# Revit family: Lockin Lockers AU_Hybrid Locker_R22
name_source: partatom
category: Furniture
units: mm (PartAtom-declared; Revit-internal decimal feet)

## family parameters
Always vertical = Yes
Cut with Voids When Loaded = No
OmniClass Number = 23.40.20.27
OmniClass Title = Storage Shelving
Render Appearance Source = Family Geometry
Room Calculation Point = No
Shared = Yes
Work Plane-Based = Yes

## types (7) — shared parameters
Base Height Control = 100 mm  [stored 0.328084 ft]
Body/Frame Material = Material - Welded Steel - Oven-Baked Powdercoat
Depth Control = 450 mm  [stored 1.47638 ft]
Desired Base Height = 100 mm  [stored 0.328084 ft]
Desired Depth = 450 mm  [stored 1.47638 ft]
Desired Height = 2100 mm
Desired Width = 400 mm  [stored 1.31234 ft]
Door Material = Material - Melamine - Laminex or Polytec Finish
Height Control = 2000 mm  [stored 6.56168 ft]
Locker Joint = 3 mm  [stored 0.00984252 ft]
Manufacturer = Lockin Lockers AU
Maximum Base Height = 100 mm  [stored 0.328084 ft]
Maximum Depth = 600 mm
Maximum Height = 2000 mm  [stored 6.56168 ft]
Maximum Width = 600 mm
Minimum Base Height = 100 mm  [stored 0.328084 ft]
Minimum Depth = 200 mm  [stored 0.656168 ft]
Minimum Height = 400 mm  [stored 1.31234 ft]
Minimum Width = 300 mm
TH Wall = 18 mm  [stored 0.0590551 ft]
URL = https://www.lockin.com.au
Width Control = 400 mm  [stored 1.31234 ft]
vis_Door 1 = Yes
zero-valued in all types: Default Elevation

## per-type parameters (varying)
| type | Description | Door Type | H Locker | Model | N_Doors | vis_Door 2 | vis_Door 3 | vis_Door 4 | vis_Door 5 | vis_Door 6 | vis_Door 7 | vis_Door 8 |
| Hybrid 8 door (HY8) | Hybrid 8 door | Lockin_Locker Door_R22 : Standard Door/Key Lock | 234.88 mm | HY8 | 8 | Yes | Yes | Yes | Yes | Yes | Yes | Yes |
| Hybrid 3 door (HY3) | Hybrid 3 door | Lockin_Locker Door_R22 : Standard Door/Key Lock | 631.33 mm | HY3 | 3 | Yes | Yes | No | No | No | No | No |
| Hybrid 4 door (HY4) | Hybrid 4 door | Lockin_Locker Door_R22 : Standard Door/Key Lock | 472.75 mm  [stored 1.55102 ft] | HY4 | 4 | Yes | Yes | Yes | No | No | No | No |
| Hybrid 6 door (HY6) | Hybrid 6 door | Lockin_Locker Door_R22 : Standard Door/Key Lock | 314.17 mm | HY6 | 6 | Yes | Yes | Yes | Yes | Yes | No | No |
| Hybrid 2 door (HY2) | Hybrid 2 door | Lockin_Locker Door_R22 : Standard Door/Key Lock | 948.5 mm  [stored 3.11188 ft] | HY2 | 2 | Yes | No | No | No | No | No | No |
| Hybrid 1 door (HY1) | Hybrid 1 door | Lockin_Locker Door_R22 : Standard Door/Key Lock | 1900 mm  [stored 6.2336 ft] | HY1 | 1 | No | No | No | No | No | No | No |
| Hybrid Wave door (HYL2) | Hybrid Wave door | Lockin_Locker Door_R22 : Wave Door/Key Lock | 1900 mm  [stored 6.2336 ft] | HYL2 | 1 | No | No | No | No | No | No | No |

note: [stored X ft] marks values corroborated as IEEE doubles in the binary element streams (Revit-internal decimal feet)

## geometry (parser evidence)
native form markers: Sweep x3
no freeform markers — native parametric forms only
